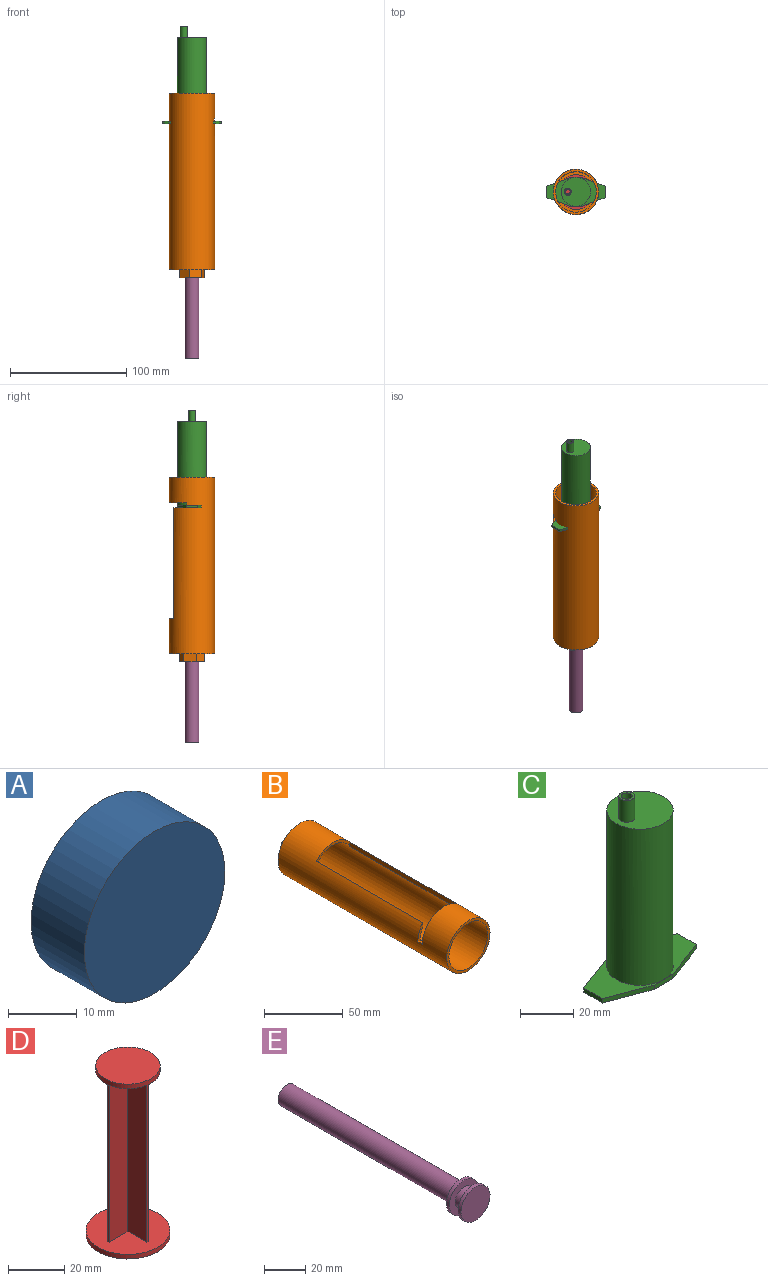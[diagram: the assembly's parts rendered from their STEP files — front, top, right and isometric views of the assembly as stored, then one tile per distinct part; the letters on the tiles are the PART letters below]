
ASSEMBLY  parts=5 mates=7
PART A: 7 faces, bbox 29x11x29 mm
  f0: cylinder r=7mm len=14mm, axis (0,-1,0), area 88mm2, adj f1,f2
  f1: plane 29x29mm, normal (0,1,0), area 506.6mm2, adj f0,f4
  f2: plane 25x25mm, normal (0,-1,0), area 336.9mm2, adj f0,f3
  f3: cylinder r=12.5mm len=25mm, axis (0,1,0), area 628.3mm2, adj f2,f5
  f4: cylinder r=14.5mm len=29mm, axis (0,1,0), area 1002.2mm2, adj f1,f6
  f5: plane 25x25mm, normal (0,1,0), area 490.9mm2, adj f3
  f6: plane 29x29mm, normal (0,-1,0), area 660.5mm2, adj f4
PART B: 23 faces, bbox 39x159x39 mm
  f0: cylinder r=17.5mm len=150mm, axis (0,1,0), area 12813.7mm2, adj f13,f14,f15,f16,f17,f18,f19,f20
  f1: cylinder r=19.5mm len=152mm, axis (0,1,0), area 15092.4mm2, adj f11,f14,f15,f16,f17,f18,f19,f20
  f2: plane 13x13mm, normal (0,-1,0), area 19.6mm2, adj f9,f12
  f3: plane 9.7x7mm, normal (-0.47,0,-0.88), area 76.8mm2, adj f4,f8,f10,f11
  f4: plane 10.96x7mm, normal (-1,0,-0.04), area 76.8mm2, adj f3,f5,f10,f11
  f5: plane 9.28x7mm, normal (-0.53,0,0.85), area 76.8mm2, adj f4,f6,f10,f11
  f6: plane 9.7x7mm, normal (0.47,0,0.88), area 76.8mm2, adj f5,f7,f10,f11
  f7: plane 10.96x7mm, normal (1,0,0.04), area 76.8mm2, adj f6,f8,f10,f11
  f8: plane 9.28x7mm, normal (0.53,0,-0.85), area 76.8mm2, adj f3,f7,f10,f11
  f9: cylinder r=6mm len=12mm, axis (0,-1,0), area 263.9mm2, adj f2,f10
  f10: plane 21.92x19.41mm, normal (0,1,0), area 199.5mm2, adj f3,f4,f5,f6,f7,f8,f9
  f11: plane 39x39mm, normal (0,1,0), area 882mm2, adj f1,f3,f4,f5,f6,f7,f8
  f12: cylinder r=6.5mm len=13mm, axis (0,1,0), area 81.7mm2, adj f2,f13
  f13: plane 35x35mm, normal (0,-1,0), area 829.4mm2, adj f0,f12
  f14: plane 39x39mm, normal (0,-1,0), area 232.5mm2, adj f0,f1
  f15: plane 30x10.49mm, normal (0,-1,0), area 70.1mm2, adj f0,f1,f16,f18
  f16: plane 96x3.45mm, normal (1,0,0), area 330.8mm2, adj f0,f1,f15,f22
  f17: plane 39x19.5mm, normal (0,1,0), area 116.2mm2, adj f0,f1,f20,f21
  f18: plane 96x3.45mm, normal (-1,0,0), area 330.8mm2, adj f0,f1,f15,f19
  f19: plane 12.46x4.5mm, normal (0,-1,0), area 23.1mm2, adj f0,f1,f18,f20
  f20: plane 4x2mm, normal (0,0,1), area 8mm2, adj f0,f1,f17,f19
  f21: plane 4x2mm, normal (0,0,1), area 8mm2, adj f0,f1,f17,f22
  f22: plane 12.46x4.5mm, normal (0,-1,0), area 23.1mm2, adj f0,f1,f16,f21
PART C: 18 faces, bbox 50x25x84 mm
  f0: cylinder r=11.5mm len=72mm, axis (0,0,-1), area 5202.5mm2, adj f11,f13
  f1: cylinder r=12.5mm len=72mm, axis (0,0,-1), area 5654.9mm2, adj f2,f12,f15
  f2: plane 25x25mm, normal (0,0,1), area 229.6mm2, adj f1,f3,f7,f8,f9,f10
  f3: plane 10x2mm, normal (0,1,0), area 20mm2, adj f2,f4,f10,f11,f12
  f4: plane 20x7.5mm, normal (0.35,0.94,0), area 42.7mm2, adj f3,f5,f11,f12
  f5: plane 10x2mm, normal (1,0,0), area 20mm2, adj f4,f6,f11,f12
  f6: plane 20x7.5mm, normal (0.35,-0.94,0), area 42.7mm2, adj f5,f7,f11,f12
  f7: plane 10x2mm, normal (0,-1,0), area 20mm2, adj f2,f6,f8,f11,f12
  f8: plane 20x7.5mm, normal (-0.35,-0.94,0), area 42.7mm2, adj f2,f7,f9,f11
  f9: plane 10x2mm, normal (-1,0,0), area 20mm2, adj f2,f8,f10,f11
  f10: plane 20x7.5mm, normal (-0.35,0.94,0), area 42.7mm2, adj f2,f3,f9,f11
  f11: plane 50x25mm, normal (0,0,-1), area 534.5mm2, adj f0,f3,f4,f5,f6,f7,f8,f9
  f12: plane 25x25mm, normal (0,0,1), area 229.6mm2, adj f1,f3,f4,f5,f6,f7
  f13: plane 23x23mm, normal (0,0,-1), area 402.9mm2, adj f0,f14
  f14: cylinder r=2mm len=12mm, axis (0,0,-1), area 150.8mm2, adj f13,f17
  f15: plane 25x25mm, normal (0,0,1), area 462.6mm2, adj f1,f16
  f16: cylinder r=3mm len=10mm, axis (0,0,-1), area 188.5mm2, adj f15,f17
  f17: plane 6x6mm, normal (0,0,1), area 15.7mm2, adj f14,f16
PART D: 18 faces, bbox 30x30x74 mm
  f0: plane 23x23mm, normal (0,0,-1), area 376.5mm2, adj f1,f3,f4,f5,f6,f7,f8,f9
  f1: cylinder r=11.5mm len=23mm, axis (0,0,1), area 144.5mm2, adj f0,f2
  f2: plane 23x23mm, normal (0,0,1), area 415.5mm2, adj f1
  f3: plane 70x9.5mm, normal (0,-1,0), area 665mm2, adj f0,f4,f14,f17
  f4: plane 70x9.5mm, normal (1,0,0), area 665mm2, adj f0,f3,f5,f17
  f5: plane 70x1mm, normal (0,-1,0), area 70mm2, adj f0,f4,f6,f17
  f6: plane 70x9.5mm, normal (-1,0,0), area 665mm2, adj f0,f5,f7,f17
  f7: plane 70x9.5mm, normal (0,-1,0), area 665mm2, adj f0,f6,f8,f17
  f8: plane 70x1mm, normal (-1,0,0), area 70mm2, adj f0,f7,f9,f17
  f9: plane 70x9.5mm, normal (0,1,0), area 665mm2, adj f0,f8,f10,f17
  f10: plane 70x9.5mm, normal (-1,0,0), area 665mm2, adj f0,f9,f11,f17
  f11: plane 70x1mm, normal (0,1,0), area 70mm2, adj f0,f10,f12,f17
  f12: plane 70x9.5mm, normal (1,0,0), area 665mm2, adj f0,f11,f13,f17
  f13: plane 70x9.5mm, normal (0,1,0), area 665mm2, adj f0,f12,f14,f17
  f14: plane 70x1mm, normal (1,0,0), area 70mm2, adj f0,f3,f13,f17
  f15: cylinder r=15mm len=30mm, axis (0,0,1), area 188.5mm2, adj f16,f17
  f16: plane 30x30mm, normal (0,0,-1), area 706.9mm2, adj f15
  f17: plane 30x30mm, normal (0,0,1), area 667.9mm2, adj f3,f4,f5,f6,f7,f8,f9,f10
PART E: 9 faces, bbox 20x130x20 mm
  f0: cylinder r=6mm len=12mm, axis (0,1,0), area 226.2mm2, adj f2,f7
  f1: cylinder r=10mm len=20mm, axis (0,1,0), area 125.7mm2, adj f2,f3
  f2: plane 20x20mm, normal (0,-1,0), area 201.1mm2, adj f0,f1
  f3: plane 20x20mm, normal (0,1,0), area 201.1mm2, adj f1,f5
  f4: plane 12x12mm, normal (0,1,0), area 113.1mm2, adj f5
  f5: cylinder r=6mm len=120mm, axis (0,1,0), area 4523.9mm2, adj f3,f4
  f6: cylinder r=10mm len=20mm, axis (0,-1,0), area 125.7mm2, adj f7,f8
  f7: plane 20x20mm, normal (0,1,0), area 201.1mm2, adj f0,f6
  f8: plane 20x20mm, normal (0,-1,0), area 314.2mm2, adj f6
PLACE A rot(axis=(-1,0,0),90deg) t=(-25,-4.82,-194.58)mm
PLACE B rot(axis=(-0.99,0.11,-0.11),90.7deg) t=(-25,-4.82,-226.58)mm
PLACE C t=(-25,-4.82,11.42)mm fixed
PLACE D t=(-25,-4.82,17.42)mm
PLACE E rot(axis=(-0.99,0.11,-0.11),90.7deg) t=(-25,-4.82,-192.58)mm
MATE planar B.f19 <-> C.f11  axis (0,0,1) through (-6.82,-3.25,9.42)mm
MATE slider E.f0 <-> B.f9  axis (0,0,-1) through (-25,-4.82,-72.58)mm
MATE cylindrical A.f0 <-> E.f0  axis (0,0,1) through (-25,-4.82,-67.58)mm
MATE planar A.f4 <-> D.f15  axis (0,0,1) through (-25,-4.82,-58.58)mm
MATE cylindrical B.f0 <-> C.f1  axis (0,0,-1) through (-25,-4.82,35.42)mm
MATE slider D.f1 <-> C.f0  axis (0,0,1) through (-25,-4.82,14.42)mm
MATE planar E.f1 <-> A.f4  axis (0,0,1) through (-25,-4.82,-70.58)mm
